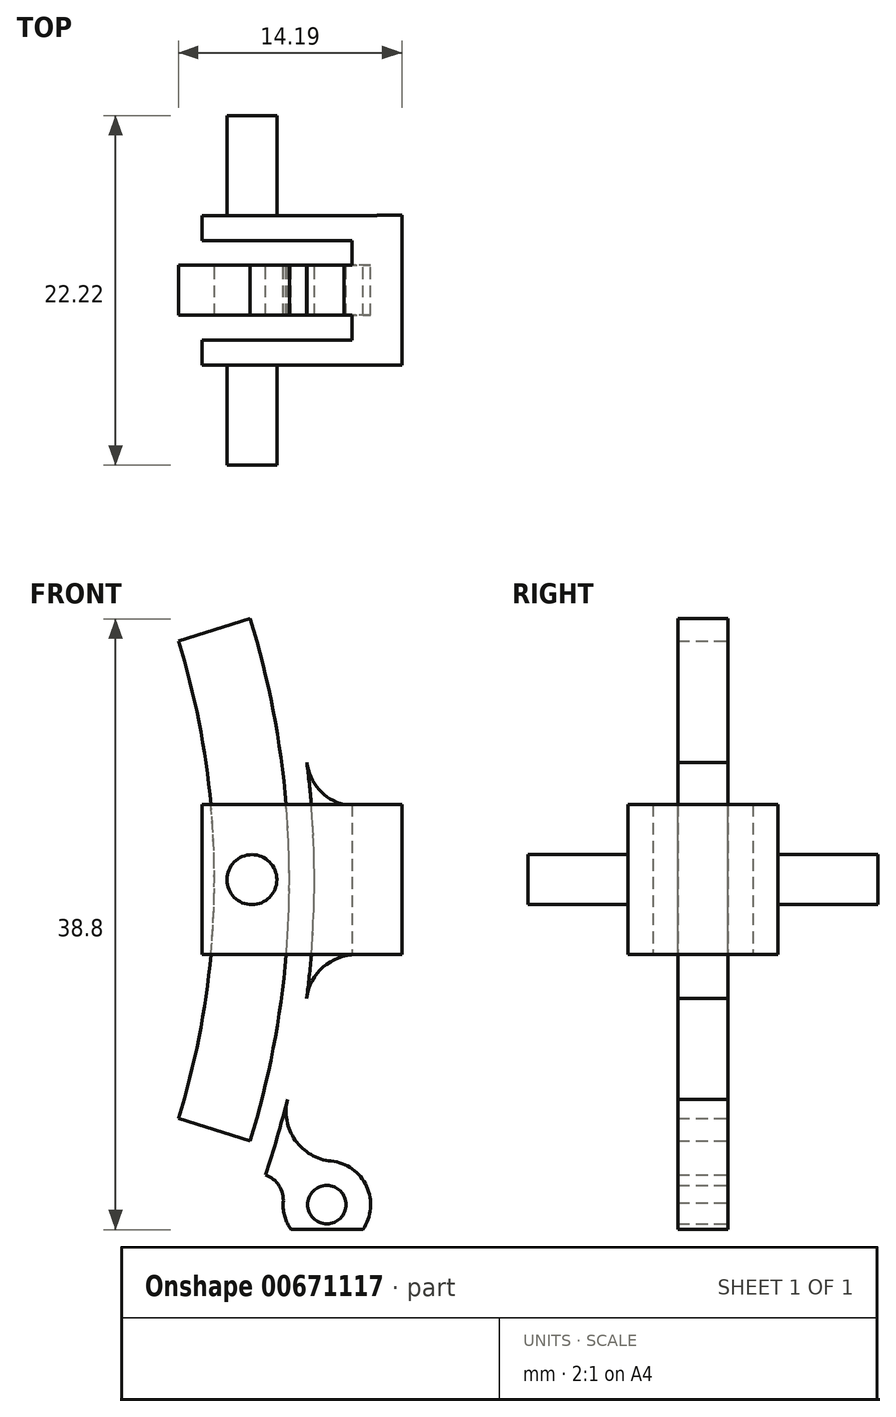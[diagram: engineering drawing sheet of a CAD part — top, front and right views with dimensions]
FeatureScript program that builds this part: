
annotation { "Feature Type Name" : "Feature", "Feature Type Description" : "" }
export const myFeature = defineFeature(function(context is Context, id is Id, definition is map)
    precondition{}
    {
        {
            var Q0;
            Q0=qCreatedBy(makeId("Front.planeOp"),FACE);
            var sketch = newSketch(context, id + "F0", { "sketchPlane" : qUnion([Q0])});
            skLineSegment(sketch, "E0.bottom", {"start": v(15.77, 52.02) * mm, "end": v(41.17, 52.02) * mm});
            skLineSegment(sketch, "E0.top", {"start": v(15.77, 7.57) * mm, "end": v(41.17, 7.57) * mm});
            skLineSegment(sketch, "E0.left", {"start": v(15.77, 52.02) * mm, "end": v(15.77, 7.57) * mm});
            skLineSegment(sketch, "E0.right", {"start": v(41.17, 52.02) * mm, "end": v(41.17, 7.57) * mm});
            skLineSegment(sketch, "E1", {"start": v(-27.75, 29.8) * mm, "end": v(53.68, 29.8) * mm, "construction": true});
            skLineSegment(sketch, "E2", {"start": v(2.64, 45.67) * mm, "end": v(53.6, 45.67) * mm, "construction": true});
            skLineSegment(sketch, "E3", {"start": v(26.22, 60.99) * mm, "end": v(26.22, 3.12) * mm, "construction": true});
            skLineSegment(sketch, "E4", {"start": v(3.94, 13.92) * mm, "end": v(54.54, 13.92) * mm, "construction": true});
            skArc(sketch, "E5", {"start": v(23.32, 12.34) * mm, "mid": v(26.22, 29.8) * mm, "end": v(23.32, 47.26) * mm, "construction": true});
            skLineSegment(sketch, "E6", {"start": v(-27.75, 29.8) * mm, "end": v(41.17, 51) * mm, "construction": true});
            skLineSegment(sketch, "E7", {"start": v(-27.75, 29.8) * mm, "end": v(41.17, 8.59) * mm, "construction": true});
            skArc(sketch, "E8", {"start": v(21.56, 44.97) * mm, "mid": v(23.84, 29.8) * mm, "end": v(21.56, 14.62) * mm});
            skArc(sketch, "E9", {"start": v(26.1, 46.37) * mm, "mid": v(28.6, 29.8) * mm, "end": v(26.1, 13.22) * mm});
            skLineSegment(sketch, "E10", {"start": v(2.1, 47.26) * mm, "end": v(50.43, 47.26) * mm, "construction": true});
            skLineSegment(sketch, "E11", {"start": v(3.95, 12.34) * mm, "end": v(47.89, 12.34) * mm, "construction": true});
            skLineSegment(sketch, "E12", {"start": v(-27.75, 29.8) * mm, "end": v(37.25, 52.02) * mm, "construction": true});
            skLineSegment(sketch, "E13", {"start": v(-27.75, 29.8) * mm, "end": v(37.25, 7.57) * mm, "construction": true});
            skArc(sketch, "E14", {"start": v(19.56, 45.98) * mm, "mid": v(22.25, 29.8) * mm, "end": v(19.56, 13.62) * mm});
            skArc(sketch, "E15", {"start": v(27.07, 48.55) * mm, "mid": v(30.2, 29.8) * mm, "end": v(27.07, 11.05) * mm});
            skLineSegment(sketch, "E16", {"start": v(21.56, 44.97) * mm, "end": v(26.1, 46.37) * mm});
            skLineSegment(sketch, "E17", {"start": v(19.56, 45.98) * mm, "end": v(27.07, 48.55) * mm});
            skLineSegment(sketch, "E18", {"start": v(21.56, 14.62) * mm, "end": v(26.1, 13.22) * mm});
            skLineSegment(sketch, "E19", {"start": v(19.56, 13.62) * mm, "end": v(27.07, 11.05) * mm});
            skLineSegment(sketch, "E20", {"start": v(30.98, 59.22) * mm, "end": v(30.98, -1.54) * mm, "construction": true});
            skCircle(sketch, "E21", {"center": v(30.98, 9.16) * mm, "radius": 1.22 * mm});
            skCircle(sketch, "E22", {"center": v(30.98, 9.16) * mm, "radius": 2.78 * mm});
            skLineSegment(sketch, "E23", {"start": v(26.22, 63.33) * mm, "end": v(26.22, -3.89) * mm, "construction": true});
            skArc(sketch, "E24", {"start": v(27.07, 11.05) * mm, "mid": v(27.95, 10.36) * mm, "end": v(28.2, 9.27) * mm});
            skArc(sketch, "E25", {"start": v(28.49, 15.85) * mm, "mid": v(28.97, 13.25) * mm, "end": v(31.26, 11.93) * mm});
            skLineSegment(sketch, "E26", {"start": v(30, 34.56) * mm, "end": v(34.16, 34.56) * mm});
            skLineSegment(sketch, "E27", {"start": v(34.16, 34.56) * mm, "end": v(34.16, 25.04) * mm});
            skLineSegment(sketch, "E28", {"start": v(34.16, 25.04) * mm, "end": v(30, 25.04) * mm});
            skArc(sketch, "E29", {"start": v(29.71, 37.23) * mm, "mid": v(30.48, 35.53) * mm, "end": v(32.08, 34.56) * mm});
            skArc(sketch, "E30", {"start": v(32.85, 25.04) * mm, "mid": v(30.75, 24.25) * mm, "end": v(29.7, 22.27) * mm});
            skSolve(sketch);
        }
        {
            var Q0;
            {var subQ0=sQuery(id+"F0.wireOp",EDGE,"E22");var subQ1=sQuery(id+"F0.wireOp",EDGE,"E0.top");var subQ2=makeQuery(id+"F0.imprint","INTERSECT",VERTEX,{"disambiguationData":[OD(0.0)],"derivedFrom":[subQ1,subQ0]});Q0=makeQuery(id+"F0.imprint","IMPRINT",FACE,{"disambiguationData":[TD([[makeQuery(id+"F0.imprint","IMPRINT",EDGE,{"disambiguationData":[TD([[subQ2,-1.0]])],"derivedFrom":subQ1}),-1.0]])]});}
            var Q1;
            Q1=makeQuery(id+"F0.imprint","IMPRINT",FACE,{"disambiguationData":[TD([[makeQuery(id+"F0.imprint","IMPRINT",EDGE,{"derivedFrom":sQuery(id+"F0.wireOp",EDGE,"E21")}),-1.0]])]});
            var Q2;
            Q2=makeQuery(id+"F0.imprint","IMPRINT",FACE,{"disambiguationData":[TD([[makeQuery(id+"F0.imprint","IMPRINT",EDGE,{"derivedFrom":sQuery(id+"F0.wireOp",EDGE,"E8")}),-1.0]])]});
            var Q3;
            {var subQ0=sQuery(id+"F0.wireOp",EDGE,"E27");Q3=makeQuery(id+"F0.imprint","IMPRINT",FACE,{"disambiguationData":[TD([[makeQuery(id+"F0.imprint","IMPRINT",EDGE,{"derivedFrom":subQ0}),-1.0]])]});}
            var Q4;
            {var subQ3=sQuery(id+"F0.wireOp",EDGE,"E29");Q4=makeQuery(id+"F0.imprint","IMPRINT",FACE,{"disambiguationData":[TD([[makeQuery(id+"F0.imprint","IMPRINT",EDGE,{"derivedFrom":subQ3}),-1.0]])]});}
            var Q5;
            {var subQ3=sQuery(id+"F0.wireOp",EDGE,"E30");Q5=makeQuery(id+"F0.imprint","IMPRINT",FACE,{"disambiguationData":[TD([[makeQuery(id+"F0.imprint","IMPRINT",EDGE,{"derivedFrom":subQ3}),-1.0]])]});}
            var Q6;
            {var subQ3=sQuery(id+"F0.wireOp",EDGE,"E25");Q6=makeQuery(id+"F0.imprint","IMPRINT",FACE,{"disambiguationData":[TD([[makeQuery(id+"F0.imprint","IMPRINT",EDGE,{"derivedFrom":subQ3}),-1.0]])]});}
            extrude(context, id + "F1", {"entities" : qUnion([Q0, Q1, Q2, Q3, Q4, Q5, Q6]), "depth" : 3.17 * mm});
        }
        {
            var Q0;
            Q0=makeQuery(id+"F1.opExtrude","SWEPT_FACE",FACE,{"disambiguationData":[OSD([sQuery(id+"F0.wireOp",EDGE,"E27")])]});
            var sketch = newSketch(context, id + "F2", { "sketchPlane" : qUnion([Q0])});
            skLineSegment(sketch, "E31", {"start": v(-6.35, 34.56) * mm, "end": v(3.18, 34.56) * mm});
            skLineSegment(sketch, "E32", {"start": v(3.18, 34.56) * mm, "end": v(3.18, 25.04) * mm});
            skLineSegment(sketch, "E33", {"start": v(3.18, 25.04) * mm, "end": v(-6.35, 25.04) * mm});
            skLineSegment(sketch, "E34", {"start": v(-6.35, 25.04) * mm, "end": v(-6.35, 34.56) * mm});
            skSolve(sketch);
        }
        {
            var Q0;
            Q0=qSketchRegion(id+"F2",true);
            extrude(context, id + "F3", {"entities" : qUnion([Q0]), "operationType" : NewBodyOperationType.ADD, "depth" : 1.59 * mm});
        }
        {
            var Q0;
            {var subQ0=sQuery(id+"F2.wireOp",EDGE,"E31");var subQ3=sQuery(id+"F2.wireOp",EDGE,"E33");var subQ4=sQuery(id+"F2.wireOp",EDGE,"E34");Q0=makeQuery(id+"F3.boolean.opBoolean","SPLIT",FACE,{"disambiguationData":[TD([makeQuery(id+"F3.opExtrude","SWEPT_FACE",FACE,{"disambiguationData":[OSD([subQ4])]})])],"derivedFrom":makeQuery(id+"F3.opExtrude","CAP_FACE",FACE,{"disambiguationData":[OSD([subQ0,sQuery(id+"F2.wireOp",EDGE,"E32"),subQ3,subQ4])],"isStart":true})});}
            var sketch = newSketch(context, id + "F4", { "sketchPlane" : qUnion([Q0])});
            skLineSegment(sketch, "E35.bottom", {"start": v(3.18, 34.56) * mm, "end": v(6.35, 34.56) * mm});
            skLineSegment(sketch, "E35.top", {"start": v(3.18, 25.04) * mm, "end": v(6.35, 25.04) * mm});
            skLineSegment(sketch, "E35.left", {"start": v(3.18, 34.56) * mm, "end": v(3.18, 25.04) * mm});
            skLineSegment(sketch, "E35.right", {"start": v(6.35, 34.56) * mm, "end": v(6.35, 25.04) * mm});
            skLineSegment(sketch, "E36.bottom", {"start": v(0, 34.56) * mm, "end": v(-3.17, 34.56) * mm});
            skLineSegment(sketch, "E36.top", {"start": v(0, 25.04) * mm, "end": v(-3.17, 25.04) * mm});
            skLineSegment(sketch, "E36.left", {"start": v(0, 34.56) * mm, "end": v(0, 25.04) * mm});
            skLineSegment(sketch, "E36.right", {"start": v(-3.17, 34.56) * mm, "end": v(-3.17, 25.04) * mm});
            skSolve(sketch);
        }
        {
            var Q0;
            Q0=qSketchRegion(id+"F4",true);
            extrude(context, id + "F5", {"entities" : qUnion([Q0]), "operationType" : NewBodyOperationType.ADD, "depth" : 1.59 * mm});
        }
        {
            var Q0;
            Q0=makeQuery(id+"F5.opExtrude","CAP_FACE",FACE,{"disambiguationData":[OSD([sQuery(id+"F4.wireOp",EDGE,"E35.bottom"),sQuery(id+"F4.wireOp",EDGE,"E35.top"),sQuery(id+"F4.wireOp",EDGE,"E35.left"),sQuery(id+"F4.wireOp",EDGE,"E35.right")])],"isStart":false});
            var sketch = newSketch(context, id + "F6", { "sketchPlane" : qUnion([Q0])});
            skLineSegment(sketch, "E37", {"start": v(4.76, 34.56) * mm, "end": v(4.76, 25.04) * mm});
            skLineSegment(sketch, "E38", {"start": v(-1.59, 34.56) * mm, "end": v(-1.59, 25.04) * mm});
            skLineSegment(sketch, "E39.0", {"start": v(0, 34.56) * mm, "end": v(-3.17, 34.56) * mm});
            skLineSegment(sketch, "E40.0.0", {"start": v(-3.17, 25.04) * mm, "end": v(0, 25.04) * mm});
            skLineSegment(sketch, "E40.0.1", {"start": v(0, 25.04) * mm, "end": v(0, 34.56) * mm});
            skLineSegment(sketch, "E40.0.3", {"start": v(-3.17, 34.56) * mm, "end": v(-3.17, 25.04) * mm});
            skLineSegment(sketch, "E41.0.0", {"start": v(6.35, 25.04) * mm, "end": v(6.35, 34.56) * mm});
            skLineSegment(sketch, "E41.0.1", {"start": v(6.35, 34.56) * mm, "end": v(3.18, 34.56) * mm});
            skLineSegment(sketch, "E41.0.2", {"start": v(3.18, 34.56) * mm, "end": v(3.18, 25.04) * mm});
            skLineSegment(sketch, "E41.0.3", {"start": v(3.18, 25.04) * mm, "end": v(6.35, 25.04) * mm});
            skSolve(sketch);
        }
        {
            var Q0;
            {var subQ0=sQuery(id+"F6.wireOp",EDGE,"E38");Q0=makeQuery(id+"F6.imprint","IMPRINT",FACE,{"disambiguationData":[TD([[makeQuery(id+"F6.imprint","IMPRINT",EDGE,{"derivedFrom":subQ0}),-1.0]])]});}
            var Q1;
            {var subQ0=sQuery(id+"F6.wireOp",EDGE,"E37");Q1=makeQuery(id+"F6.imprint","IMPRINT",FACE,{"disambiguationData":[TD([[makeQuery(id+"F6.imprint","IMPRINT",EDGE,{"derivedFrom":subQ0}),1.0]])]});}
            extrude(context, id + "F7", {"entities" : qUnion([Q0, Q1]), "operationType" : NewBodyOperationType.ADD, "depth" : 9.52 * mm});
        }
        {
            var Q0;
            Q0=makeQuery(id+"F7.boolean.opBoolean","MERGE",FACE,{"derivedFrom":[makeQuery(id+"F5.boolean.opBoolean","MERGE",FACE,{"derivedFrom":[makeQuery(id+"F3.opExtrude","SWEPT_FACE",FACE,{"disambiguationData":[OSD([sQuery(id+"F2.wireOp",EDGE,"E34")])]}),makeQuery(id+"F5.opExtrude","SWEPT_FACE",FACE,{"disambiguationData":[OSD([sQuery(id+"F4.wireOp",EDGE,"E35.right")])]})]}),makeQuery(id+"F7.opExtrude","SWEPT_FACE",FACE,{"disambiguationData":[OSD([sQuery(id+"F6.wireOp",EDGE,"E41.0.0")])]})]});
            var sketch = newSketch(context, id + "F8", { "sketchPlane" : qUnion([Q0])});
            skCircle(sketch, "E42", {"center": v(26.22, 29.8) * mm, "radius": 1.59 * mm});
            skSolve(sketch);
        }
        {
            var Q0;
            Q0=qSketchRegion(id+"F8",true);
            extrude(context, id + "F9", {"entities" : qUnion([Q0]), "operationType" : NewBodyOperationType.ADD, "depth" : 6.35 * mm});
        }
        {
            var Q0;
            Q0=makeQuery(id+"F7.boolean.opBoolean","MERGE",FACE,{"derivedFrom":[makeQuery(id+"F5.opExtrude","SWEPT_FACE",FACE,{"disambiguationData":[OSD([sQuery(id+"F4.wireOp",EDGE,"E36.right")])]}),makeQuery(id+"F7.opExtrude","SWEPT_FACE",FACE,{"disambiguationData":[OSD([sQuery(id+"F6.wireOp",EDGE,"E40.0.3")])]})]});
            var sketch = newSketch(context, id + "F10", { "sketchPlane" : qUnion([Q0])});
            skCircle(sketch, "E43", {"center": v(-26.22, 29.8) * mm, "radius": 1.59 * mm});
            skSolve(sketch);
        }
        {
            var Q0;
            Q0=qSketchRegion(id+"F10",true);
            extrude(context, id + "F11", {"entities" : qUnion([Q0]), "operationType" : NewBodyOperationType.ADD, "depth" : 6.35 * mm});
        }
    });
